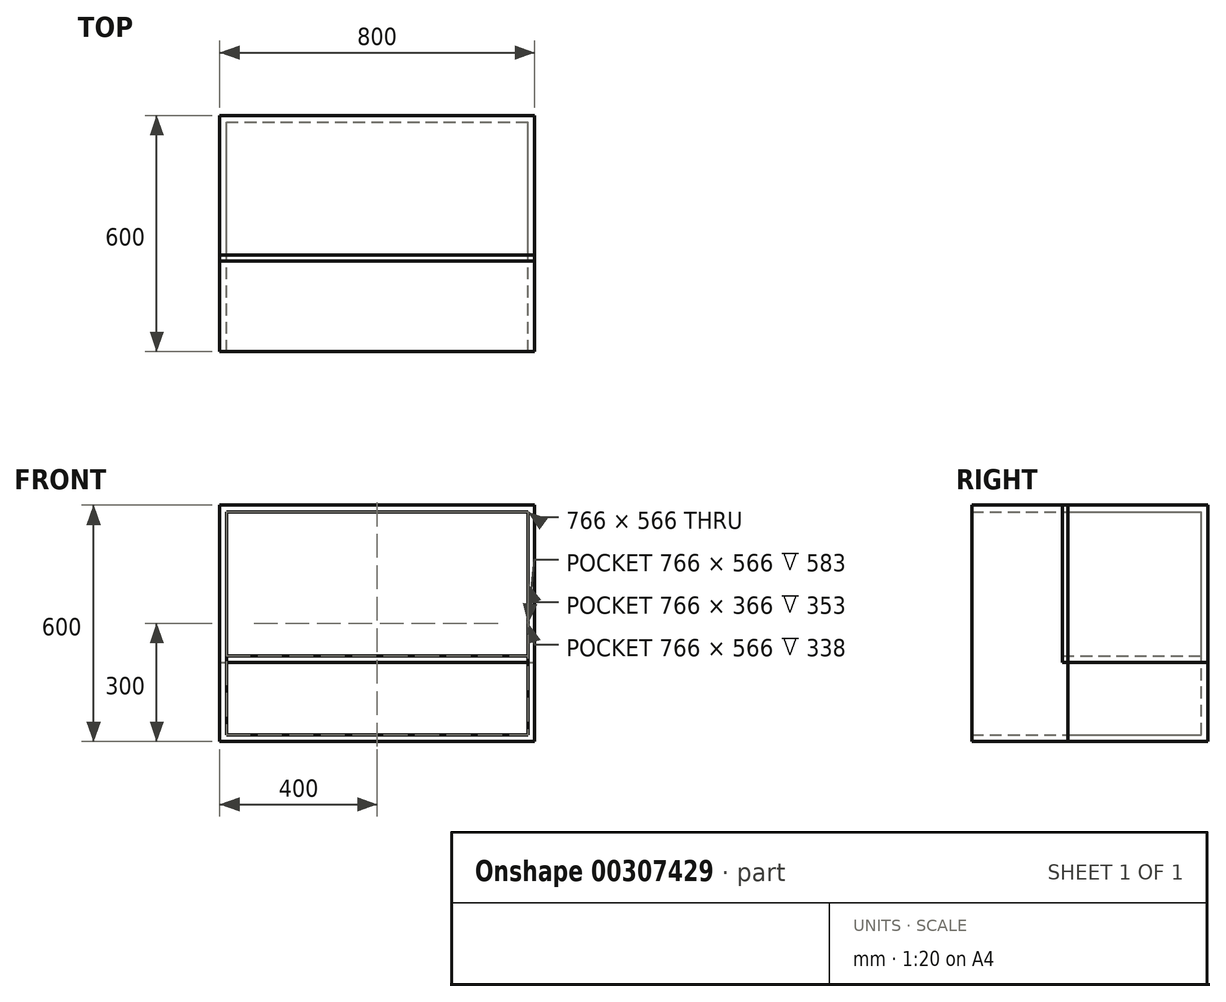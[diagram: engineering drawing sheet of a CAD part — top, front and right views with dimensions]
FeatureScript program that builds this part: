
annotation { "Feature Type Name" : "Feature", "Feature Type Description" : "" }
export const myFeature = defineFeature(function(context is Context, id is Id, definition is map)
    precondition{}
    {
        {
            var Q0;
            Q0=qCreatedBy(makeId("Front.planeOp"),FACE);
            var sketch = newSketch(context, id + "F0", { "sketchPlane" : qUnion([Q0])});
            skLineSegment(sketch, "E0.bottom", {"start": v(0, 0) * mm, "end": v(800, 0) * mm});
            skLineSegment(sketch, "E0.top", {"start": v(0, -600) * mm, "end": v(800, -600) * mm});
            skLineSegment(sketch, "E0.left", {"start": v(0, -600) * mm, "end": v(0, 0) * mm});
            skLineSegment(sketch, "E0.right", {"start": v(800, -600) * mm, "end": v(800, 0) * mm});
            skSolve(sketch);
        }
        {
            var Q0;
            Q0=makeQuery(id+"F0.imprint","IMPRINT",FACE,{"disambiguationData":[TD([[makeQuery(id+"F0.imprint","IMPRINT",EDGE,{"derivedFrom":sQuery(id+"F0.wireOp",EDGE,"E0.bottom")}),-1.0]])]});
            extrude(context, id + "F1", {"entities" : qUnion([Q0]), "depth" : 355 * mm, "offsetDistance" : 25 * mm});
        }
        {
            var Q0;
            Q0=makeQuery(id+"F1.opExtrude","CAP_FACE",FACE,{"disambiguationData":[OSD([sQuery(id+"F0.wireOp",EDGE,"E0.bottom"),sQuery(id+"F0.wireOp",EDGE,"E0.top"),sQuery(id+"F0.wireOp",EDGE,"E0.left"),sQuery(id+"F0.wireOp",EDGE,"E0.right")])],"isStart":false});
            shell(context, id + "F2", {"entities" : qUnion([Q0]), "thickness" : 17 * mm});
        }
        {
            var Q0;
            Q0=qCreatedBy(makeId("Front.planeOp"),FACE);
            var sketch = newSketch(context, id + "F3", { "sketchPlane" : qUnion([Q0])});
            skLineSegment(sketch, "E1.0", {"start": v(0, 0) * mm, "end": v(800, 0) * mm});
            skLineSegment(sketch, "E2.0", {"start": v(0, -600) * mm, "end": v(0, 0) * mm});
            skLineSegment(sketch, "E3.0", {"start": v(800, -600) * mm, "end": v(800, 0) * mm});
            skLineSegment(sketch, "E4", {"start": v(0, -600) * mm, "end": v(800, -600) * mm});
            skLineSegment(sketch, "E5", {"start": v(0, -400) * mm, "end": v(800, -400) * mm});
            skSolve(sketch);
        }
        {
            var Q0;
            Q0=makeQuery(id+"F3.imprint","IMPRINT",FACE,{"disambiguationData":[TD([[makeQuery(id+"F3.imprint","IMPRINT",EDGE,{"derivedFrom":sQuery(id+"F3.wireOp",EDGE,"E1.0")}),-1.0]])]});
            extrude(context, id + "F4", {"entities" : qUnion([Q0]), "depth" : 370 * mm, "offsetDistance" : 25 * mm});
        }
        {
            var Q0;
            Q0=makeQuery(id+"F4.opExtrude","CAP_FACE",FACE,{"disambiguationData":[OSD([sQuery(id+"F3.wireOp",EDGE,"E1.0"),sQuery(id+"F3.wireOp",EDGE,"E2.0"),sQuery(id+"F3.wireOp",EDGE,"E3.0"),sQuery(id+"F3.wireOp",EDGE,"E5")])],"isStart":false});
            shell(context, id + "F5", {"entities" : qUnion([Q0]), "thickness" : 17 * mm});
        }
        {
            var Q0;
            Q0 = qSketchRegion(id + "F3", true);
            extrude(context, id + "F6", {"entities" : qUnion([Q0]), "depth" : 600 * mm, "offsetDistance" : 25 * mm});
        }
        {
            var Q0;
            Q0=makeQuery(id+"F6.opExtrude","CAP_FACE",FACE,{"disambiguationData":[OSD([sQuery(id+"F3.wireOp",EDGE,"E1.0"),sQuery(id+"F3.wireOp",EDGE,"E2.0"),sQuery(id+"F3.wireOp",EDGE,"E3.0"),sQuery(id+"F3.wireOp",EDGE,"E4")])],"isStart":false});
            shell(context, id + "F7", {"entities" : qUnion([Q0]), "thickness" : 17 * mm});
        }
    });
